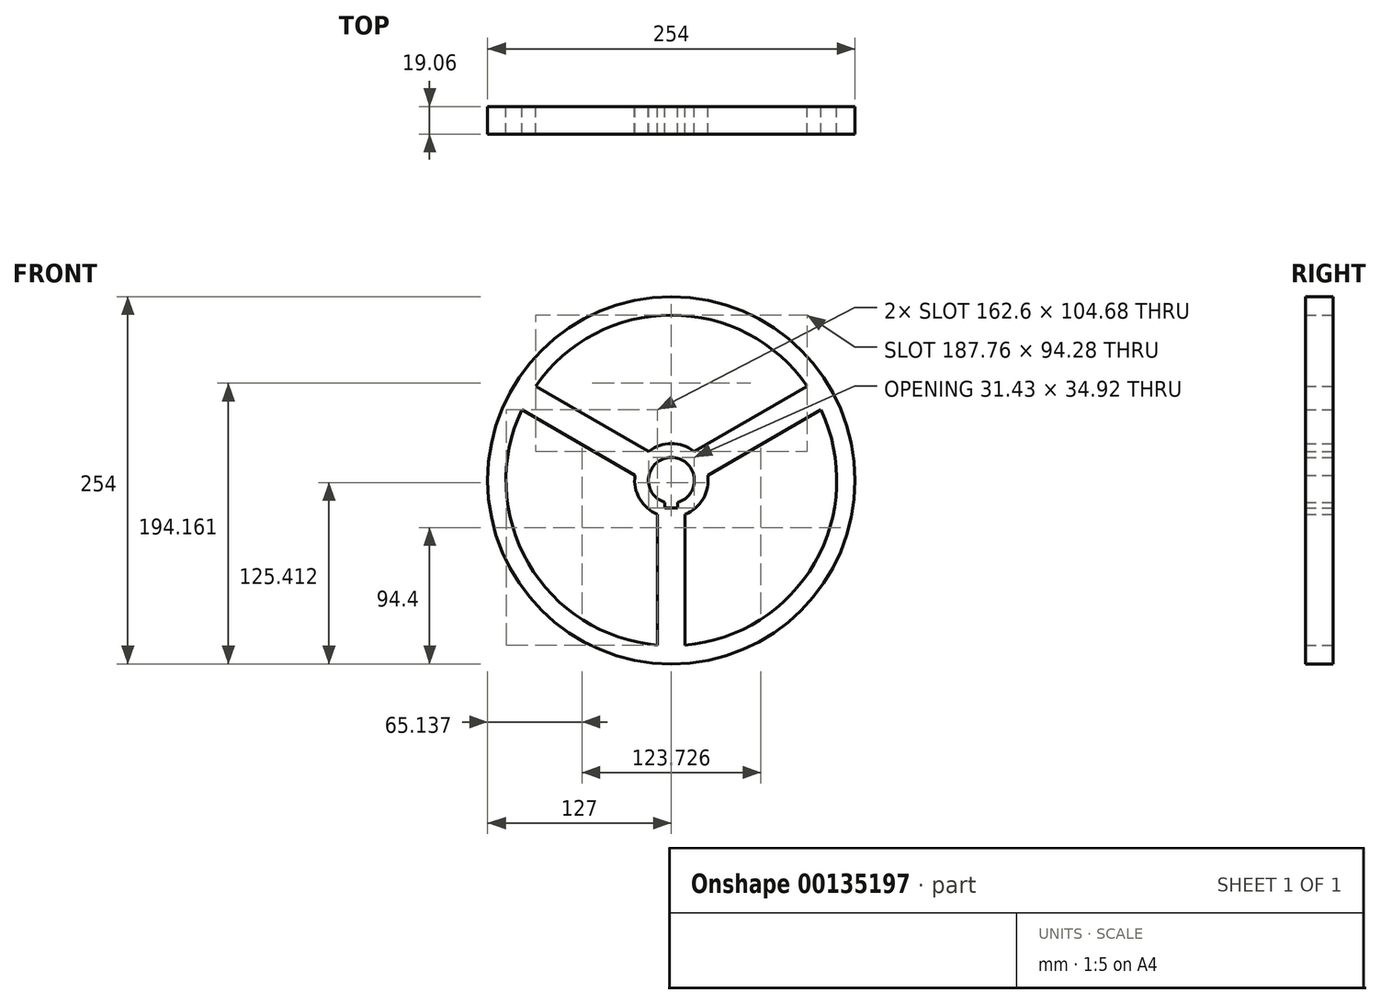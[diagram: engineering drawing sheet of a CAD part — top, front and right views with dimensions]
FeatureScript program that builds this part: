
annotation { "Feature Type Name" : "Feature", "Feature Type Description" : "" }
export const myFeature = defineFeature(function(context is Context, id is Id, definition is map)
    precondition{}
    {
        {
            var Q0;
            Q0=qCreatedBy(makeId("Front.planeOp"),FACE);
            var sketch = newSketch(context, id + "F0", { "sketchPlane" : qUnion([Q0])});
            skCircle(sketch, "E0", {"center": v(0, 0) * mm, "radius": 25.4 * mm});
            skLineSegment(sketch, "E1", {"start": v(4.45, -15.24) * mm, "end": v(4.45, -19.05) * mm});
            skLineSegment(sketch, "E2", {"start": v(-4.45, -15.24) * mm, "end": v(-4.45, -19.05) * mm});
            skLineSegment(sketch, "E3", {"start": v(-4.45, -19.05) * mm, "end": v(4.45, -19.05) * mm});
            skArc(sketch, "E4", {"start": v(4.45, -15.24) * mm, "mid": v(0, 15.88) * mm, "end": v(-4.45, -15.24) * mm});
            skPoint(sketch, "E4.first.point", {"position": v(-4.45, -15.24) * mm});
            skPoint(sketch, "E4.second.point", {"position": v(4.45, -15.24) * mm});
            skPoint(sketch, "E4.third.point", {"position": v(0.62, 15.86) * mm});
            skCircle(sketch, "E5", {"center": v(0, 0) * mm, "radius": 114.3 * mm});
            skPoint(sketch, "E6", {"position": v(-9.53, -113.9) * mm});
            skPoint(sketch, "E7", {"position": v(9.53, -113.9) * mm});
            skLineSegment(sketch, "E8", {"start": v(-9.52, -113.9) * mm, "end": v(-9.52, -23.55) * mm});
            skLineSegment(sketch, "E9", {"start": v(9.52, -113.9) * mm, "end": v(9.52, -23.55) * mm});
            skLineSegment(sketch, "E10.1.0", {"start": v(93.88, 65.2) * mm, "end": v(15.63, 20.02) * mm});
            skLineSegment(sketch, "E10.1.1", {"start": v(103.4, 48.7) * mm, "end": v(25.15, 3.52) * mm});
            skLineSegment(sketch, "E10.2.0", {"start": v(-103.4, 48.7) * mm, "end": v(-25.15, 3.52) * mm});
            skLineSegment(sketch, "E10.2.1", {"start": v(-93.88, 65.2) * mm, "end": v(-15.63, 20.02) * mm});
            skCircle(sketch, "E11", {"center": v(0, 0) * mm, "radius": 127 * mm});
            skSolve(sketch);
        }
        {
            var Q0;
            Q0=makeQuery(id+"F0.imprint","IMPRINT",FACE,{"disambiguationData":[TD([[makeQuery(id+"F0.imprint","IMPRINT",EDGE,{"derivedFrom":sQuery(id+"F0.wireOp",EDGE,"E11")}),1.0]])]});
            extrude(context, id + "F1", {"entities" : qUnion([Q0]), "endBound" : BoundingType.SYMMETRIC, "depth" : 19.05 * mm});
        }
        {
            var Q0;
            {var subQ0=sQuery(id+"F0.wireOp",EDGE,"E8");Q0=makeQuery(id+"F0.imprint","IMPRINT",FACE,{"disambiguationData":[TD([[makeQuery(id+"F0.imprint","IMPRINT",EDGE,{"derivedFrom":subQ0}),-1.0]])]});}
            var Q1;
            {var subQ0=sQuery(id+"F0.wireOp",EDGE,"E10.1.0");Q1=makeQuery(id+"F0.imprint","IMPRINT",FACE,{"disambiguationData":[TD([[makeQuery(id+"F0.imprint","IMPRINT",EDGE,{"derivedFrom":subQ0}),1.0]])]});}
            var Q2;
            {var subQ0=sQuery(id+"F0.wireOp",EDGE,"E10.2.0");Q2=makeQuery(id+"F0.imprint","IMPRINT",FACE,{"disambiguationData":[TD([[makeQuery(id+"F0.imprint","IMPRINT",EDGE,{"derivedFrom":subQ0}),1.0]])]});}
            extrude(context, id + "F2", {"entities" : qUnion([Q0, Q1, Q2]), "operationType" : NewBodyOperationType.ADD, "endBound" : BoundingType.SYMMETRIC, "depth" : 19.05 * mm});
        }
        {
            var Q0;
            Q0=makeQuery(id+"F0.imprint","IMPRINT",FACE,{"disambiguationData":[TD([[makeQuery(id+"F0.imprint","IMPRINT",EDGE,{"derivedFrom":sQuery(id+"F0.wireOp",EDGE,"E1")}),1.0]])]});
            extrude(context, id + "F3", {"entities" : qUnion([Q0]), "operationType" : NewBodyOperationType.ADD, "endBound" : BoundingType.SYMMETRIC, "depth" : 19.05 * mm});
        }
    });
